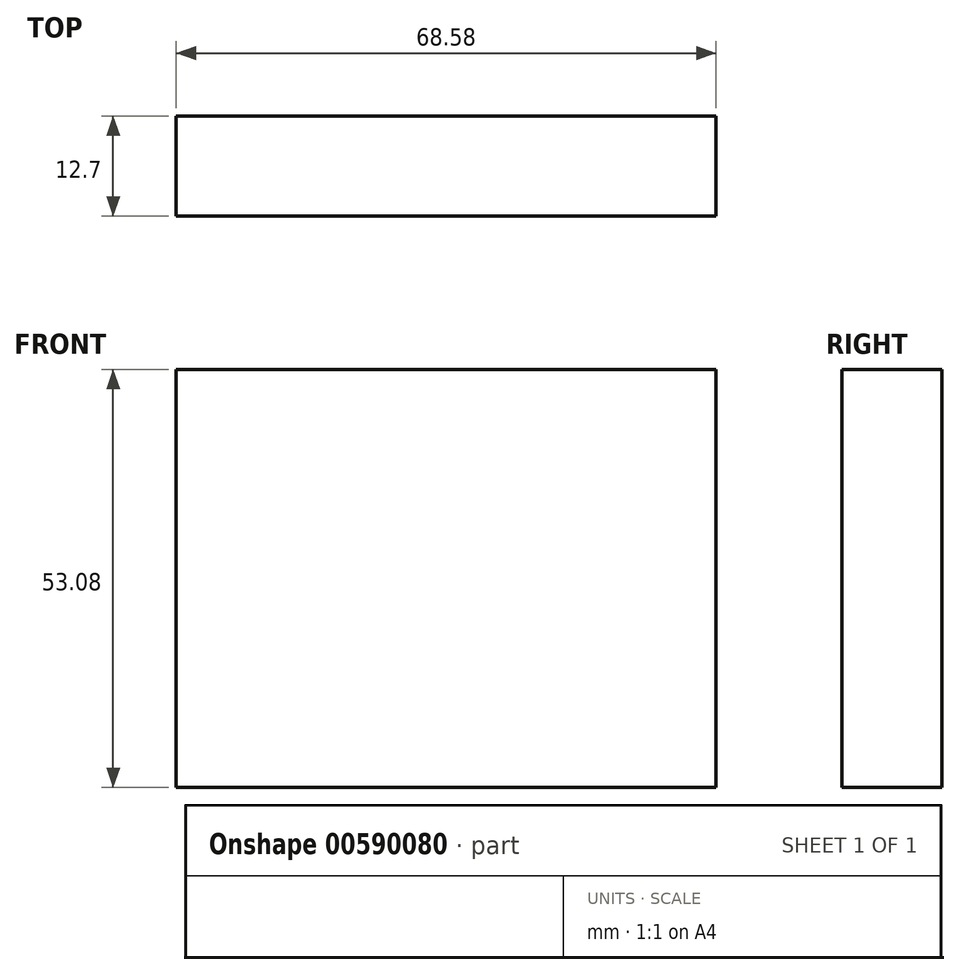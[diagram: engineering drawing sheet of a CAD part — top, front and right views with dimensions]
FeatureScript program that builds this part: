
annotation { "Feature Type Name" : "Feature", "Feature Type Description" : "" }
export const myFeature = defineFeature(function(context is Context, id is Id, definition is map)
    precondition{}
    {
        {
            var Q0;
            Q0=qCreatedBy(makeId("Front.planeOp"),FACE);
            var sketch = newSketch(context, id + "F0", { "sketchPlane" : qUnion([Q0])});
            skLineSegment(sketch, "E0.bottom", {"start": v(-46.33, 37.27) * mm, "end": v(22.25, 37.27) * mm});
            skLineSegment(sketch, "E0.top", {"start": v(-46.33, -15.81) * mm, "end": v(22.25, -15.81) * mm});
            skLineSegment(sketch, "E0.left", {"start": v(-46.33, 37.27) * mm, "end": v(-46.33, -15.81) * mm});
            skLineSegment(sketch, "E0.right", {"start": v(22.25, 37.27) * mm, "end": v(22.25, -15.81) * mm});
            skSolve(sketch);
        }
        {
            var Q0;
            Q0=makeQuery(id+"F0.imprint","IMPRINT",FACE,{"disambiguationData":[TD([[makeQuery(id+"F0.imprint","IMPRINT",EDGE,{"derivedFrom":sQuery(id+"F0.wireOp",EDGE,"E0.bottom")}),-1.0]])]});
            extrude(context, id + "F1", {"entities" : qUnion([Q0]), "depth" : 12.7 * mm, "offsetDistance" : 25.4 * mm});
        }
    });
